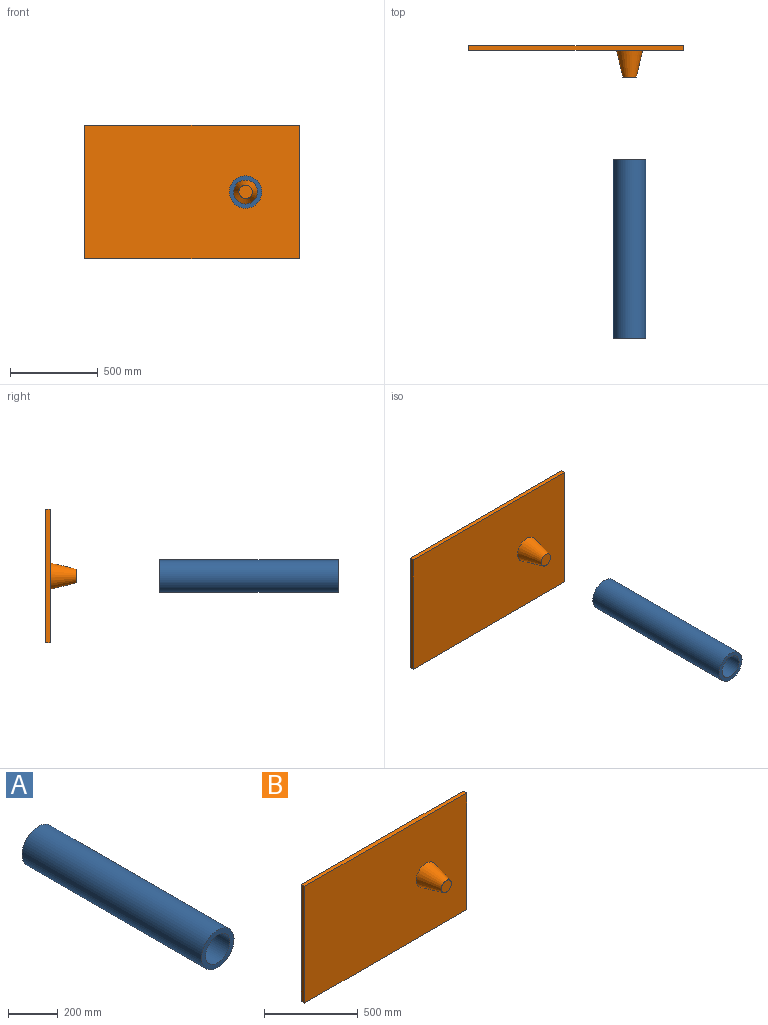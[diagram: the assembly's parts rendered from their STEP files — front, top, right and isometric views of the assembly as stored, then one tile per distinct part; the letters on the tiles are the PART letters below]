
ASSEMBLY  parts=2 mates=1
PART A: 4 faces, bbox 184.2x1016x184.2 mm
  f0: cylinder r=68.26mm len=1016mm, axis (0,1,0), area 435768.4mm2, adj f2,f3
  f1: cylinder r=92.08mm len=1016mm, axis (0,1,0), area 587780.7mm2, adj f2,f3
  f2: plane 184.15x184.15mm, normal (0,-1,0), area 11994.7mm2, adj f0,f1
  f3: plane 184.15x184.15mm, normal (0,1,0), area 11994.7mm2, adj f0,f1
PART B: 8 faces, bbox 1219.2x177.8x762 mm
  f0: plane 1219.2x25.4mm, normal (0,0,1), area 30967.7mm2, adj f1,f3,f4,f5
  f1: plane 762x25.4mm, normal (-1,0,0), area 19354.8mm2, adj f0,f2,f4,f5
  f2: plane 1219.2x25.4mm, normal (0,0,-1), area 30967.7mm2, adj f1,f3,f4,f5
  f3: plane 762x25.4mm, normal (1,0,0), area 19354.8mm2, adj f0,f2,f4,f5
  f4: plane 1219.2x762mm, normal (0,-1,0), area 911541.1mm2, adj f0,f1,f2,f3,f7
  f5: plane 1219.2x762mm, normal (0,1,0), area 929030.4mm2, adj f0,f1,f2,f3
  f6: plane 76.2x76.2mm, normal (0,-1,0), area 4560.4mm2, adj f7
  f7: cone r=74.61mm half-angle=13.5deg, axis (0,1,0), area 55491.5mm2, adj f4,f6
PLACE A rot(axis=(0,-1,0),21.7deg) t=(-50.32,-747.47,66.46)mm
PLACE B t=(-50.32,-99.5,66.46)mm fixed
MATE cylindrical A.f1 <-> B.f7  axis (0,1,0) through (-50.32,-1255.47,66.46)mm
